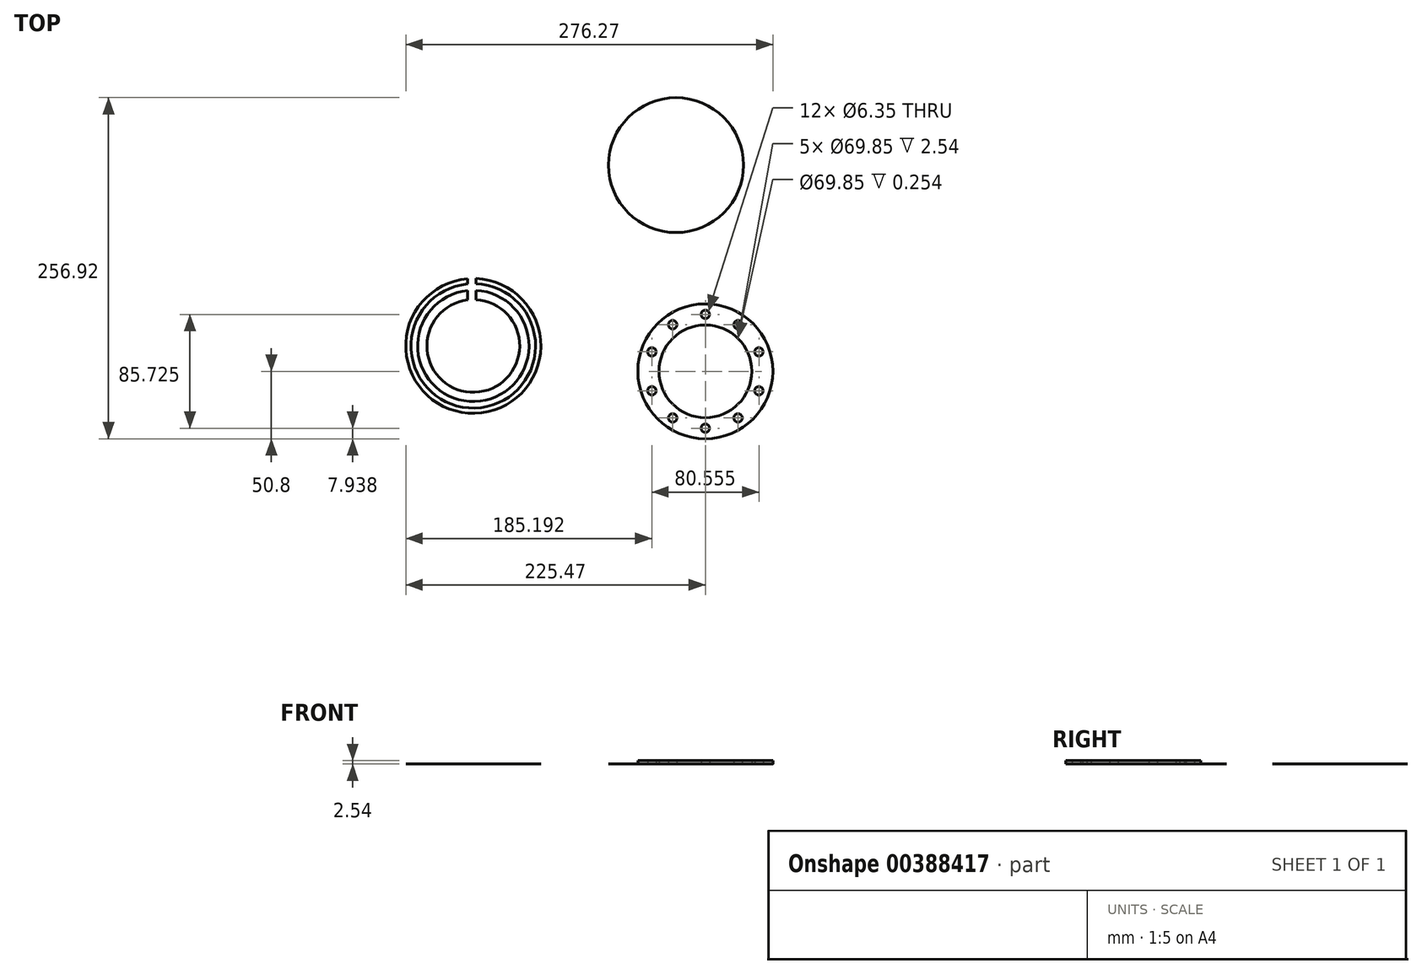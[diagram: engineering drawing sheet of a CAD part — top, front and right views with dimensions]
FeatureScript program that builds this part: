
annotation { "Feature Type Name" : "Feature", "Feature Type Description" : "" }
export const myFeature = defineFeature(function(context is Context, id is Id, definition is map)
    precondition{}
    {
        {
            var Q0;
            Q0=qCreatedBy(makeId("Top.planeOp"),FACE);
            var sketch = newSketch(context, id + "F0", { "sketchPlane" : qUnion([Q0])});
            skCircle(sketch, "E0", {"center": v(0, 0) * mm, "radius": 50.8 * mm});
            skCircle(sketch, "E1", {"center": v(0, 0) * mm, "radius": 34.93 * mm});
            skCircle(sketch, "E2", {"center": v(0, 42.86) * mm, "radius": 3.18 * mm});
            skCircle(sketch, "E3", {"center": v(0, 0) * mm, "radius": 34.97 * mm, "construction": true});
            skLineSegment(sketch, "E4", {"start": v(-50.8, 0) * mm, "end": v(50.8, 0) * mm, "construction": true});
            skCircle(sketch, "E5.MirrorC", {"center": v(0, -42.86) * mm, "radius": 3.18 * mm});
            skSolve(sketch);
        }
        {
            var Q0;
            Q0=makeQuery(id+"F0.imprint","IMPRINT",FACE,{"disambiguationData":[TD([[makeQuery(id+"F0.imprint","IMPRINT",EDGE,{"derivedFrom":sQuery(id+"F0.wireOp",EDGE,"E2")}),1.0]])]});
            extrude(context, id + "F1", {"entities" : qUnion([Q0]), "depth" : 2.54 * mm});
        }
        {
            var Q0;
            Q0=makeQuery(id+"F1.opExtrude","SWEPT_BODY",BODY,{"disambiguationData":[OSD([sQuery(id+"F0.wireOp",EDGE,"E2")])]});
            var Q1;
            Q1=sQuery(id+"F0.wireOp",EDGE,"E1");
            circularPattern(context, id + "F2", {"entities" : qUnion([Q0]), "axis" : qUnion([Q1]), "angle" : 35 * degree, "instanceCount" : 3});
        }
        {
            var Q0;
            Q0=makeQuery(id+"F1.opExtrude","SWEPT_BODY",BODY,{"disambiguationData":[OSD([sQuery(id+"F0.wireOp",EDGE,"E2")])]});
            var Q1;
            Q1=sQuery(id+"F0.wireOp",EDGE,"E1");
            circularPattern(context, id + "F3", {"entities" : qUnion([Q0]), "axis" : qUnion([Q1]), "angle" : 70 * degree, "instanceCount" : 3, "oppositeDirection" : true, "equalSpace" : true});
        }
        {
            var Q0;
            Q0=makeQuery(id+"F0.imprint","IMPRINT",FACE,{"disambiguationData":[TD([[makeQuery(id+"F0.imprint","IMPRINT",EDGE,{"derivedFrom":sQuery(id+"F0.wireOp",EDGE,"E5.MirrorC")}),-1.0]])]});
            extrude(context, id + "F4", {"entities" : qUnion([Q0]), "depth" : 2.54 * mm});
        }
        {
            var Q0;
            Q0=makeQuery(id+"F4.opExtrude","SWEPT_BODY",BODY,{"disambiguationData":[OSD([sQuery(id+"F0.wireOp",EDGE,"E5.MirrorC")])]});
            var Q1;
            Q1=sQuery(id+"F0.wireOp",EDGE,"E1");
            circularPattern(context, id + "F5", {"entities" : qUnion([Q0]), "axis" : qUnion([Q1]), "angle" : 70 * degree, "instanceCount" : 3, "equalSpace" : true});
        }
        {
            var Q0;
            Q0=makeQuery(id+"F4.opExtrude","SWEPT_BODY",BODY,{"disambiguationData":[OSD([sQuery(id+"F0.wireOp",EDGE,"E5.MirrorC")])]});
            var Q1;
            Q1=sQuery(id+"F0.wireOp",EDGE,"E1");
            circularPattern(context, id + "F6", {"entities" : qUnion([Q0]), "axis" : qUnion([Q1]), "angle" : 70 * degree, "instanceCount" : 3, "oppositeDirection" : true, "equalSpace" : true});
        }
        {
            var Q0;
            Q0=makeQuery(id+"F0.imprint","IMPRINT",FACE,{"disambiguationData":[TD([[makeQuery(id+"F0.imprint","IMPRINT",EDGE,{"derivedFrom":sQuery(id+"F0.wireOp",EDGE,"E0")}),1.0]])]});
            extrude(context, id + "F7", {"entities" : qUnion([Q0]), "depth" : 0.25 * mm});
        }
        {
            var Q0;
            Q0=qCreatedBy(makeId("Top.planeOp"),FACE);
            var sketch = newSketch(context, id + "F8", { "sketchPlane" : qUnion([Q0])});
            skCircle(sketch, "E6", {"center": v(-174.67, 19.13) * mm, "radius": 50.8 * mm});
            skCircle(sketch, "E7", {"center": v(-174.67, 19.13) * mm, "radius": 34.93 * mm});
            skCircle(sketch, "E8", {"center": v(-174.67, 19.13) * mm, "radius": 46.85 * mm});
            skCircle(sketch, "E9", {"center": v(-174.67, 19.13) * mm, "radius": 41.91 * mm});
            skLineSegment(sketch, "E10", {"start": v(-179.03, 53.78) * mm, "end": v(-179.03, 69.74) * mm});
            skLineSegment(sketch, "E11", {"start": v(-172.68, 54) * mm, "end": v(-172.68, 69.9) * mm});
            skSolve(sketch);
        }
        {
            var Q0;
            {var subQ0=sQuery(id+"F8.wireOp",EDGE,"E10");var subQ1=sQuery(id+"F8.wireOp",EDGE,"E7");var subQ2=makeQuery(id+"F8.imprint","INTERSECT",VERTEX,{"derivedFrom":[subQ1,subQ0]});Q0=makeQuery(id+"F8.imprint","IMPRINT",FACE,{"disambiguationData":[TD([[makeQuery(id+"F8.imprint","IMPRINT",EDGE,{"disambiguationData":[TD([[subQ2,-1.0]])],"derivedFrom":subQ1}),-1.0]])]});}
            var Q1;
            {var subQ0=sQuery(id+"F8.wireOp",EDGE,"E10");var subQ1=sQuery(id+"F8.wireOp",EDGE,"E6");var subQ2=makeQuery(id+"F8.imprint","INTERSECT",VERTEX,{"derivedFrom":[subQ1,subQ0]});Q1=makeQuery(id+"F8.imprint","IMPRINT",FACE,{"disambiguationData":[TD([[makeQuery(id+"F8.imprint","IMPRINT",EDGE,{"disambiguationData":[TD([[subQ2,-1.0]])],"derivedFrom":subQ1}),1.0]])]});}
            extrude(context, id + "F9", {"entities" : qUnion([Q0, Q1]), "depth" : 0.25 * mm});
        }
        {
            var Q0;
            Q0=qCreatedBy(makeId("Top.planeOp"),FACE);
            var sketch = newSketch(context, id + "F10", { "sketchPlane" : qUnion([Q0])});
            skCircle(sketch, "E12", {"center": v(-22.1, 155.32) * mm, "radius": 50.8 * mm});
            skSolve(sketch);
        }
        {
            var Q0;
            Q0=makeQuery(id+"F10.imprint","IMPRINT",FACE,{"disambiguationData":[TD([[makeQuery(id+"F10.imprint","IMPRINT",EDGE,{"derivedFrom":sQuery(id+"F10.wireOp",EDGE,"E12")}),1.0]])]});
            extrude(context, id + "F11", {"entities" : qUnion([Q0]), "depth" : 0.25 * mm});
        }
    });
